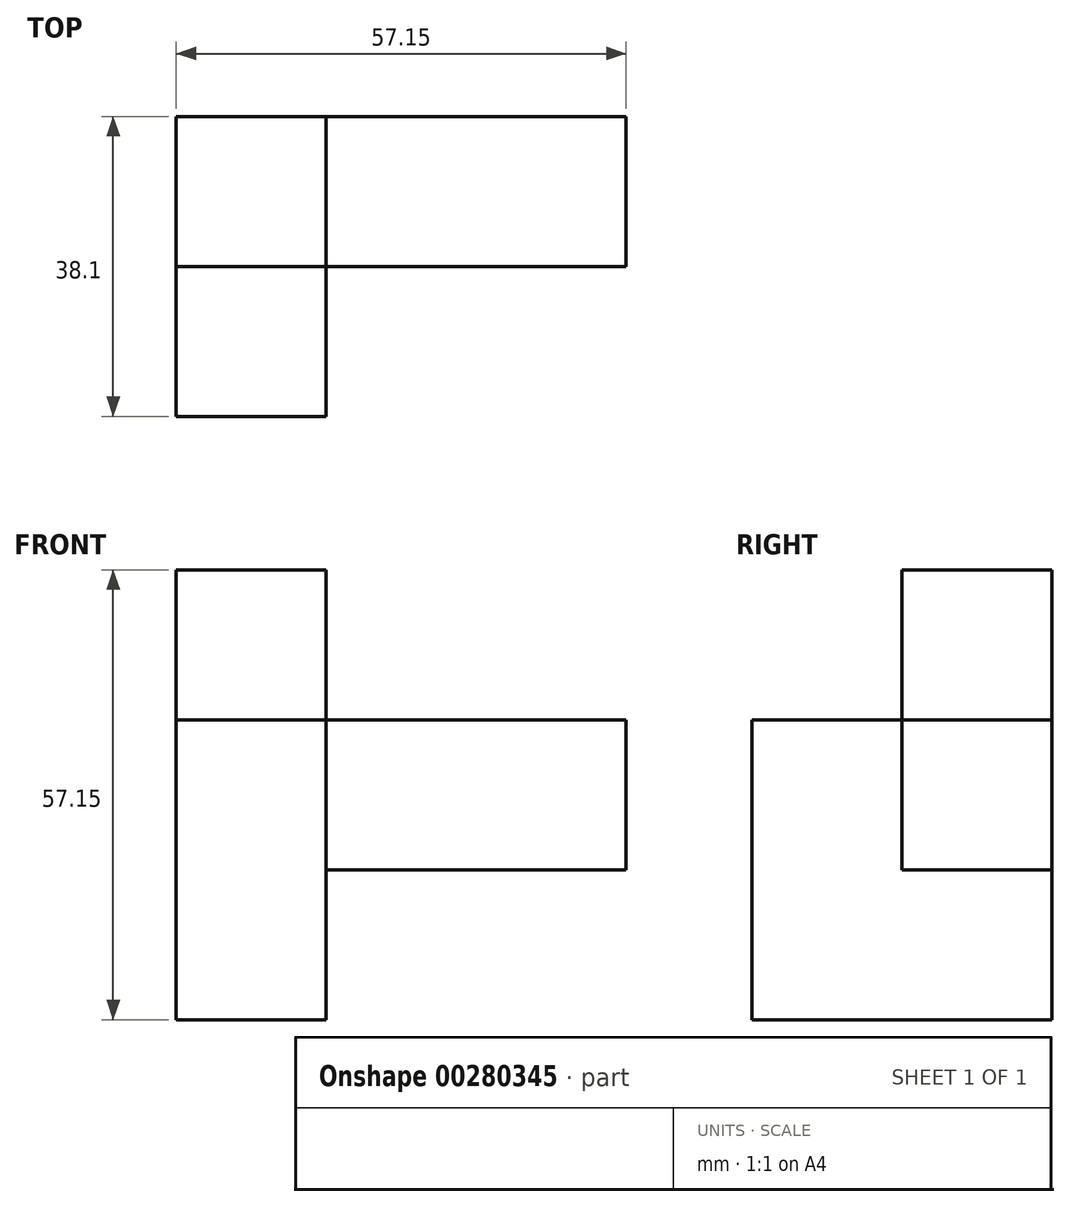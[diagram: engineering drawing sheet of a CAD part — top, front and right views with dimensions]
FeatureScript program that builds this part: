
annotation { "Feature Type Name" : "Feature", "Feature Type Description" : "" }
export const myFeature = defineFeature(function(context is Context, id is Id, definition is map)
    precondition{}
    {
        {
            var Q0;
            Q0=qCreatedBy(makeId("Top.planeOp"),FACE);
            var sketch = newSketch(context, id + "F0", { "sketchPlane" : qUnion([Q0])});
            skLineSegment(sketch, "E0.bottom", {"start": v(0, 0) * mm, "end": v(19.05, 0) * mm});
            skLineSegment(sketch, "E0.top", {"start": v(0, 38.1) * mm, "end": v(19.05, 38.1) * mm});
            skLineSegment(sketch, "E0.left", {"start": v(0, 0) * mm, "end": v(0, 38.1) * mm});
            skLineSegment(sketch, "E0.right", {"start": v(19.05, 0) * mm, "end": v(19.05, 38.1) * mm});
            skSolve(sketch);
        }
        {
            var Q0;
            Q0 = qSketchRegion(id + "F0", true);
            extrude(context, id + "F1", {"entities" : qUnion([Q0]), "depth" : 57.15 * mm});
        }
        {
            var Q0;
            Q0=makeQuery(id+"F1.opExtrude","CAP_FACE",FACE,{"disambiguationData":[OSD([sQuery(id+"F0.wireOp",EDGE,"E0.bottom"),sQuery(id+"F0.wireOp",EDGE,"E0.top"),sQuery(id+"F0.wireOp",EDGE,"E0.left"),sQuery(id+"F0.wireOp",EDGE,"E0.right")])],"isStart":false});
            var sketch = newSketch(context, id + "F2", { "sketchPlane" : qUnion([Q0])});
            skLineSegment(sketch, "E1.bottom", {"start": v(0, 0) * mm, "end": v(19.05, 0) * mm});
            skLineSegment(sketch, "E1.top", {"start": v(0, 19.05) * mm, "end": v(19.05, 19.05) * mm});
            skLineSegment(sketch, "E1.left", {"start": v(0, 0) * mm, "end": v(0, 19.05) * mm});
            skLineSegment(sketch, "E1.right", {"start": v(19.05, 0) * mm, "end": v(19.05, 19.05) * mm});
            skSolve(sketch);
        }
        {
            var Q0;
            Q0 = qSketchRegion(id + "F2", true);
            extrude(context, id + "F3", {"entities" : qUnion([Q0]), "operationType" : NewBodyOperationType.REMOVE, "oppositeDirection" : true, "depth" : 19.05 * mm});
        }
        {
            var Q0;
            Q0=makeQuery(id+"F1.opExtrude","SWEPT_FACE",FACE,{"disambiguationData":[OSD([sQuery(id+"F0.wireOp",EDGE,"E0.right")])]});
            var sketch = newSketch(context, id + "F4", { "sketchPlane" : qUnion([Q0])});
            skLineSegment(sketch, "E2.bottom", {"start": v(19.05, 38.1) * mm, "end": v(38.1, 38.1) * mm});
            skLineSegment(sketch, "E2.top", {"start": v(19.05, 19.05) * mm, "end": v(38.1, 19.05) * mm});
            skLineSegment(sketch, "E2.left", {"start": v(19.05, 38.1) * mm, "end": v(19.05, 19.05) * mm});
            skLineSegment(sketch, "E2.right", {"start": v(38.1, 38.1) * mm, "end": v(38.1, 19.05) * mm});
            skSolve(sketch);
        }
        {
            var Q0;
            Q0 = qSketchRegion(id + "F4", true);
            extrude(context, id + "F5", {"entities" : qUnion([Q0]), "operationType" : NewBodyOperationType.ADD, "depth" : 38.1 * mm});
        }
    });
